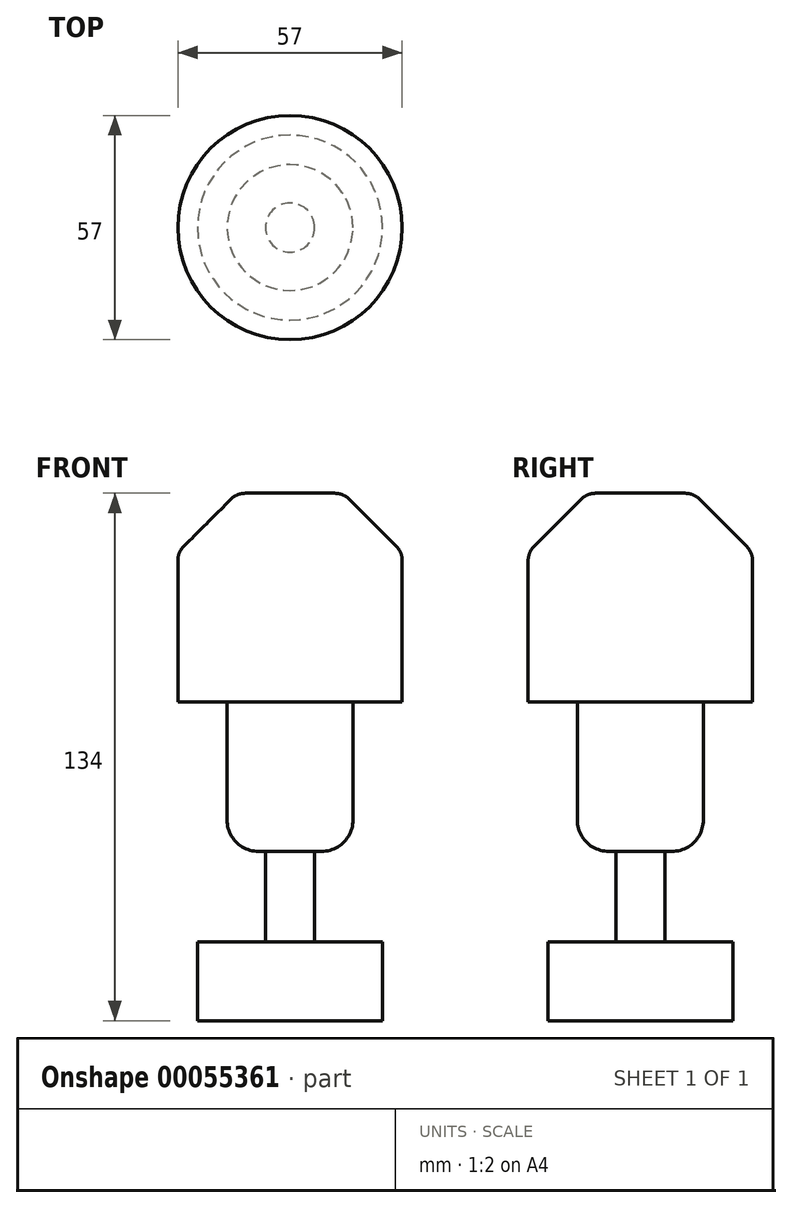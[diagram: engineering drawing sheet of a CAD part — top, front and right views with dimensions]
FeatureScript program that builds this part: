
annotation { "Feature Type Name" : "Feature", "Feature Type Description" : "" }
export const myFeature = defineFeature(function(context is Context, id is Id, definition is map)
    precondition{}
    {
        {
            var Q0;
            Q0=qCreatedBy(makeId("Top.planeOp"),FACE);
            var sketch = newSketch(context, id + "F0", { "sketchPlane" : qUnion([Q0])});
            skCircle(sketch, "E0", {"center": v(0, 0) * mm, "radius": 28.5 * mm});
            skSolve(sketch);
        }
        {
            var Q0;
            Q0=qSketchRegion(id+"F0",true);
            extrude(context, id + "F1", {"entities" : qUnion([Q0]), "endBound" : BoundingType.SYMMETRIC, "depth" : 53 * mm});
        }
        {
            var Q0;
            Q0=makeQuery(id+"F1.opExtrude","CAP_FACE",FACE,{"disambiguationData":[OSD([sQuery(id+"F0.wireOp",EDGE,"E0")])],"isStart":true});
            var sketch = newSketch(context, id + "F2", { "sketchPlane" : qUnion([Q0])});
            skCircle(sketch, "E1", {"center": v(0, 0) * mm, "radius": 16 * mm});
            skSolve(sketch);
        }
        {
            var Q0;
            Q0=qSketchRegion(id+"F2",true);
            extrude(context, id + "F3", {"entities" : qUnion([Q0]), "operationType" : NewBodyOperationType.ADD, "depth" : 38 * mm});
        }
        {
            var Q0;
            Q0=makeQuery(id+"F3.opExtrude","CAP_EDGE",EDGE,{"disambiguationData":[OSD([sQuery(id+"F2.wireOp",EDGE,"E1")])],"isStart":false});
            fillet(context, id + "F4", {"entities" : qUnion([Q0]), "radius" : 8 * mm, "tangentPropagation" : true, "allowEdgeOverflow" : false});
        }
        {
            var Q0;
            Q0=makeQuery(id+"F1.opExtrude","CAP_EDGE",EDGE,{"disambiguationData":[OSD([sQuery(id+"F0.wireOp",EDGE,"E0")])],"isStart":false});
            chamfer(context, id + "F5", {"entities" : qUnion([Q0]), "width" : 15 * mm, "tangentPropagation" : true});
        }
        {
            var Q0;
            {var subQ0=sQuery(id+"F0.wireOp",EDGE,"E0");Q0=makeQuery(id+"F5.opChamfer","BLEND_EDGE",EDGE,{"blendedFrom":[makeQuery(id+"F1.opExtrude","CAP_EDGE",EDGE,{"disambiguationData":[OSD([subQ0])],"isStart":false}),makeQuery(id+"F1.opExtrude","SWEPT_FACE",FACE,{"disambiguationData":[OSD([subQ0])]})],"blendedInto":[makeQuery(id+"F1.opExtrude","SWEPT_FACE",FACE,{"disambiguationData":[OSD([subQ0])]})]});}
            var Q1;
            {var subQ0=sQuery(id+"F0.wireOp",EDGE,"E0");Q1=makeQuery(id+"F5.opChamfer","BLEND_EDGE",EDGE,{"blendedFrom":[makeQuery(id+"F1.opExtrude","CAP_EDGE",EDGE,{"disambiguationData":[OSD([subQ0])],"isStart":false}),makeQuery(id+"F1.opExtrude","CAP_FACE",FACE,{"disambiguationData":[OSD([subQ0])],"isStart":false})],"blendedInto":[makeQuery(id+"F1.opExtrude","CAP_FACE",FACE,{"disambiguationData":[OSD([subQ0])],"isStart":false})]});}
            fillet(context, id + "F6", {"entities" : qUnion([Q0, Q1]), "radius" : 5 * mm, "tangentPropagation" : true, "allowEdgeOverflow" : false});
        }
        {
            var Q0;
            Q0=makeQuery(id+"F3.opExtrude","CAP_FACE",FACE,{"disambiguationData":[OSD([sQuery(id+"F2.wireOp",EDGE,"E1")])],"isStart":false});
            var sketch = newSketch(context, id + "F7", { "sketchPlane" : qUnion([Q0])});
            skCircle(sketch, "E2", {"center": v(0, 0) * mm, "radius": 6.25 * mm});
            skSolve(sketch);
        }
        {
            var Q0;
            Q0=qSketchRegion(id+"F7",true);
            extrude(context, id + "F8", {"entities" : qUnion([Q0]), "operationType" : NewBodyOperationType.ADD, "depth" : 23 * mm});
        }
        {
            var Q0;
            Q0=makeQuery(id+"F8.opExtrude","CAP_FACE",FACE,{"disambiguationData":[OSD([sQuery(id+"F7.wireOp",EDGE,"E2")])],"isStart":false});
            var sketch = newSketch(context, id + "F9", { "sketchPlane" : qUnion([Q0])});
            skCircle(sketch, "E3", {"center": v(0, 0) * mm, "radius": 23.5 * mm});
            skSolve(sketch);
        }
        {
            var Q0;
            Q0=qSketchRegion(id+"F9",true);
            extrude(context, id + "F10", {"entities" : qUnion([Q0]), "operationType" : NewBodyOperationType.ADD, "depth" : 20 * mm});
        }
    });
